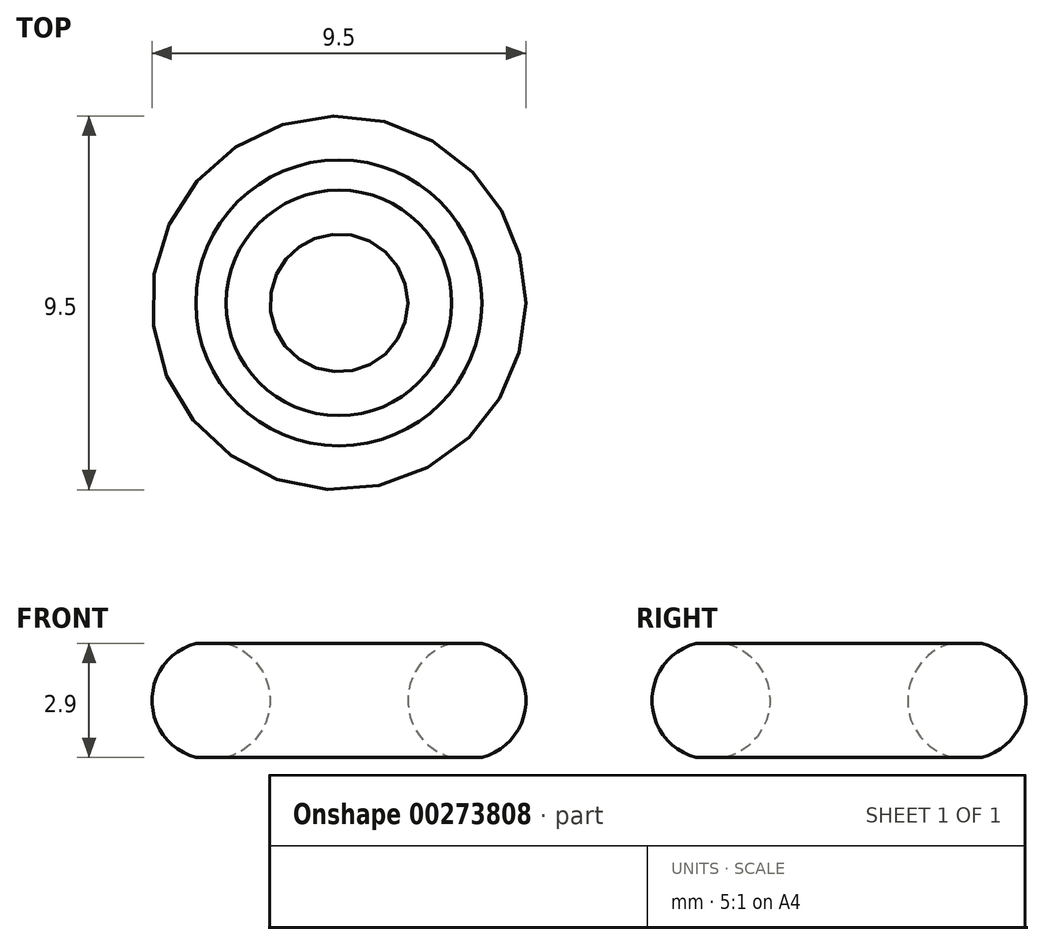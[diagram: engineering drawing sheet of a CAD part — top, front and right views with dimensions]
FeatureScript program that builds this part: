
annotation { "Feature Type Name" : "Feature", "Feature Type Description" : "" }
export const myFeature = defineFeature(function(context is Context, id is Id, definition is map)
    precondition{}
    {
        {
            var Q0;
            Q0=qCreatedBy(makeId("Front.planeOp"),FACE);
            var sketch = newSketch(context, id + "F0", { "sketchPlane" : qUnion([Q0])});
            skCircle(sketch, "E0", {"center": v(-3.25, 0) * mm, "radius": 1.5 * mm});
            skLineSegment(sketch, "E1", {"start": v(-3.25, 0) * mm, "end": v(0, 0) * mm});
            skLineSegment(sketch, "E2", {"start": v(-3.63, 1.45) * mm, "end": v(-2.87, 1.45) * mm});
            skLineSegment(sketch, "E3", {"start": v(-3.25, 0) * mm, "end": v(-3.25, 1.45) * mm});
            skLineSegment(sketch, "E4.MirrorCS", {"start": v(-3.63, -1.45) * mm, "end": v(-2.87, -1.45) * mm});
            skPoint(sketch, "E5", {"position": v(-1.75, 0) * mm});
            skSolve(sketch);
        }
        {
            var Q0;
            Q0=qCreatedBy(makeId("Front.planeOp"),FACE);
            var sketch = newSketch(context, id + "F1", { "sketchPlane" : qUnion([Q0])});
            skLineSegment(sketch, "E6", {"start": v(0, 2.87) * mm, "end": v(0, -3.21) * mm});
            skSolve(sketch);
        }
        {
            var Q0;
            Q0=makeQuery(id+"F0.imprint","IMPRINT",FACE,{"disambiguationData":[TD([[makeQuery(id+"F0.imprint","IMPRINT",EDGE,{"derivedFrom":sQuery(id+"F0.wireOp",EDGE,"E0")}),1.0]])]});
            var Q1;
            {var subQ5=sQuery(id+"F0.wireOp",EDGE,"E3");Q1=makeQuery(id+"F0.imprint","IMPRINT",FACE,{"disambiguationData":[TD([[makeQuery(id+"F0.imprint","IMPRINT",EDGE,{"derivedFrom":subQ5}),-1.0]])]});}
            var Q2;
            Q2 = qSketchRegion(id + "F1", true);
            var Q3;
            Q3=sQuery(id+"F1.wireOp",EDGE,"E6");
            revolve(context, id + "F2", {"surfaceOperationType" : NewSurfaceOperationType.NEW, "entities" : qUnion([Q0, Q1, Q2]), "axis" : qUnion([Q3]), "revolveType" : RevolveType.FULL});
        }
    });
